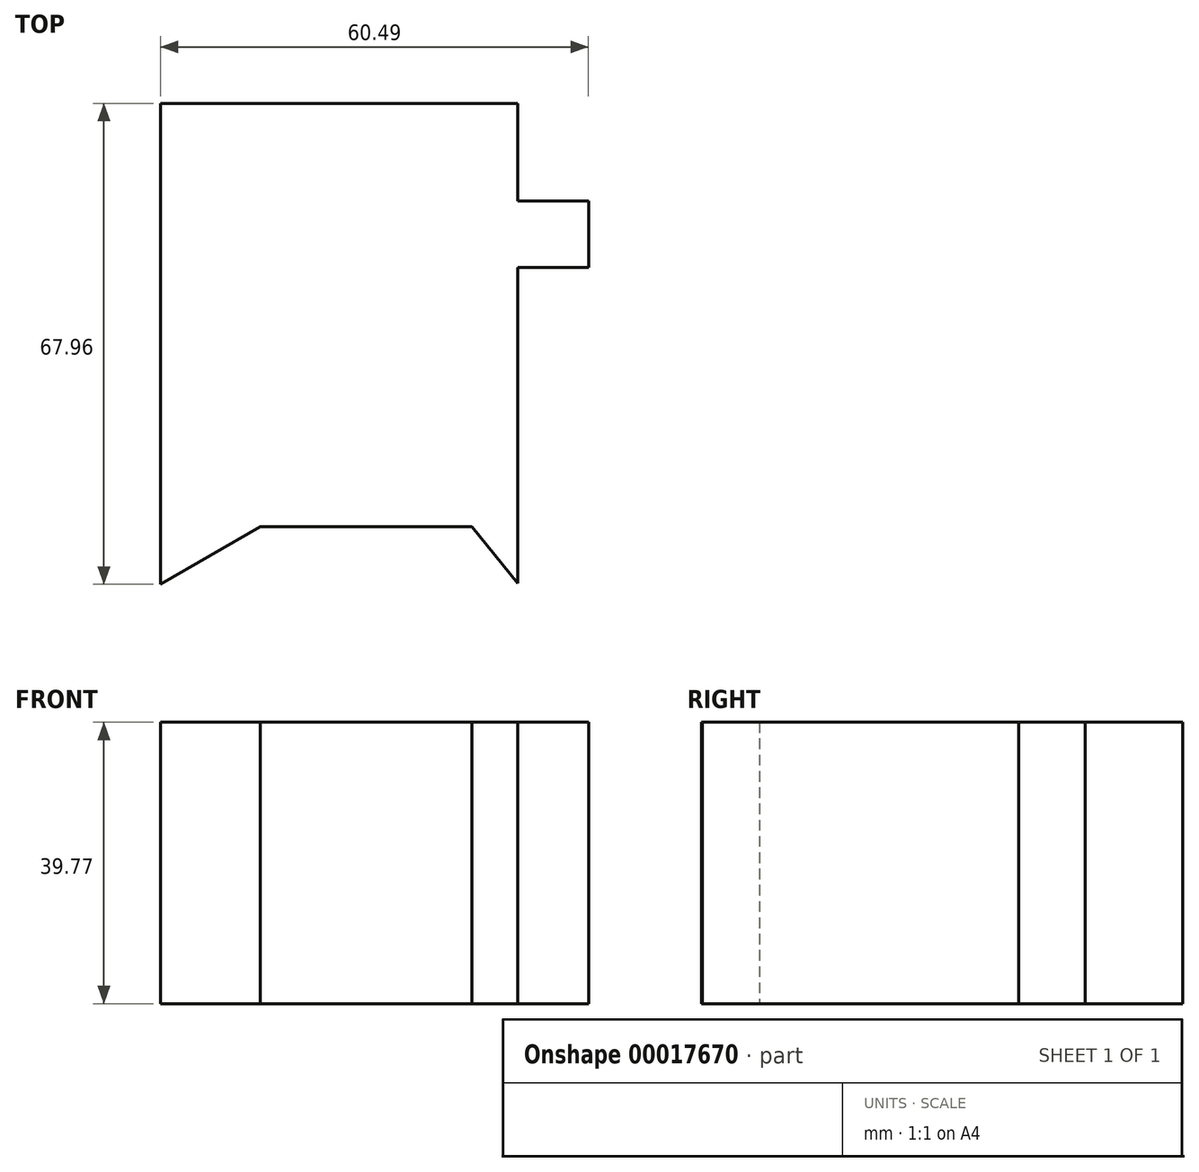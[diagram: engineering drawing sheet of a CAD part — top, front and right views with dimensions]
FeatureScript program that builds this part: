
annotation { "Feature Type Name" : "Feature", "Feature Type Description" : "" }
export const myFeature = defineFeature(function(context is Context, id is Id, definition is map)
    precondition{}
    {
        {
            var Q0;
            Q0=qCreatedBy(makeId("Top.planeOp"),FACE);
            var sketch = newSketch(context, id + "F0", { "sketchPlane" : qUnion([Q0])});
            skLineSegment(sketch, "E0", {"start": v(-25.37, 18.21) * mm, "end": v(25.15, 18.21) * mm});
            skLineSegment(sketch, "E1", {"start": v(25.15, 18.21) * mm, "end": v(25.15, 4.45) * mm});
            skLineSegment(sketch, "E2", {"start": v(25.15, 4.45) * mm, "end": v(35.12, 4.45) * mm});
            skLineSegment(sketch, "E3", {"start": v(35.12, 4.45) * mm, "end": v(35.12, -4.97) * mm});
            skLineSegment(sketch, "E4", {"start": v(35.12, -4.97) * mm, "end": v(25.15, -4.97) * mm});
            skLineSegment(sketch, "E5", {"start": v(25.15, -4.97) * mm, "end": v(25.15, -49.63) * mm});
            skLineSegment(sketch, "E6", {"start": v(25.15, -49.63) * mm, "end": v(18.62, -41.6) * mm});
            skLineSegment(sketch, "E7", {"start": v(18.62, -41.6) * mm, "end": v(-11.26, -41.6) * mm});
            skLineSegment(sketch, "E8", {"start": v(-11.26, -41.6) * mm, "end": v(-25.37, -49.75) * mm});
            skLineSegment(sketch, "E9", {"start": v(-25.37, -49.75) * mm, "end": v(-25.37, 18.21) * mm});
            skSolve(sketch);
        }
        {
            var Q0;
            Q0=makeQuery(id+"F0.imprint","IMPRINT",FACE,{"disambiguationData":[TD([[makeQuery(id+"F0.imprint","IMPRINT",EDGE,{"derivedFrom":sQuery(id+"F0.wireOp",EDGE,"E0")}),-1.0]])]});
            extrude(context, id + "F1", {"entities" : qUnion([Q0]), "depth" : 25.4 * mm});
        }
        {
            var Q0;
            Q0=makeQuery(id+"F1.opExtrude","CAP_FACE",FACE,{"disambiguationData":[OSD([sQuery(id+"F0.wireOp",EDGE,"E0"),sQuery(id+"F0.wireOp",EDGE,"E1"),sQuery(id+"F0.wireOp",EDGE,"E2"),sQuery(id+"F0.wireOp",EDGE,"E3"),sQuery(id+"F0.wireOp",EDGE,"E4"),sQuery(id+"F0.wireOp",EDGE,"E5"),sQuery(id+"F0.wireOp",EDGE,"E6"),sQuery(id+"F0.wireOp",EDGE,"E7"),sQuery(id+"F0.wireOp",EDGE,"E8"),sQuery(id+"F0.wireOp",EDGE,"E9")])],"isStart":false});
            extrude(context, id + "F2", {"entities" : qUnion([Q0]), "operationType" : NewBodyOperationType.ADD, "depth" : 14.37 * mm});
        }
    });
